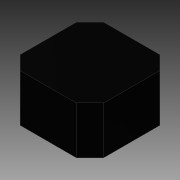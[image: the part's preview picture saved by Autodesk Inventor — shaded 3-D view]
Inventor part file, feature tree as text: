
AUTODESK INVENTOR PART (.ipt)
format: ipt  version: 2015 (Build 190159000, 159)  size: 75,264 bytes
history: native  units: mm
features: reference x8, extrude x1, sketch x1
ambient origin geometry x8: Origin, YZ Plane, XZ Plane, XY Plane, X Axis, Y Axis, Z Axis, Center Point
bodies: Solid1 (feature_tree)
feature tree (10):
  extrude  "Extrusion1"  [1 undecoded]
  sketch  "Sketch1"  dims[d0=24.0mm d1=0.0mm]
  reference  "Reference1"
  reference  "Reference2"
  reference  "Reference3"
  reference  "Reference4"
  reference  "Reference5"
  reference  "Reference6"
  reference  "Reference7"
  reference  "Reference8"
note: 1 required parameter value undecoded (feature->parameter linkage not recoverable at this tier; creation-order binding heuristic only, values carry confidence <= 0.55)
